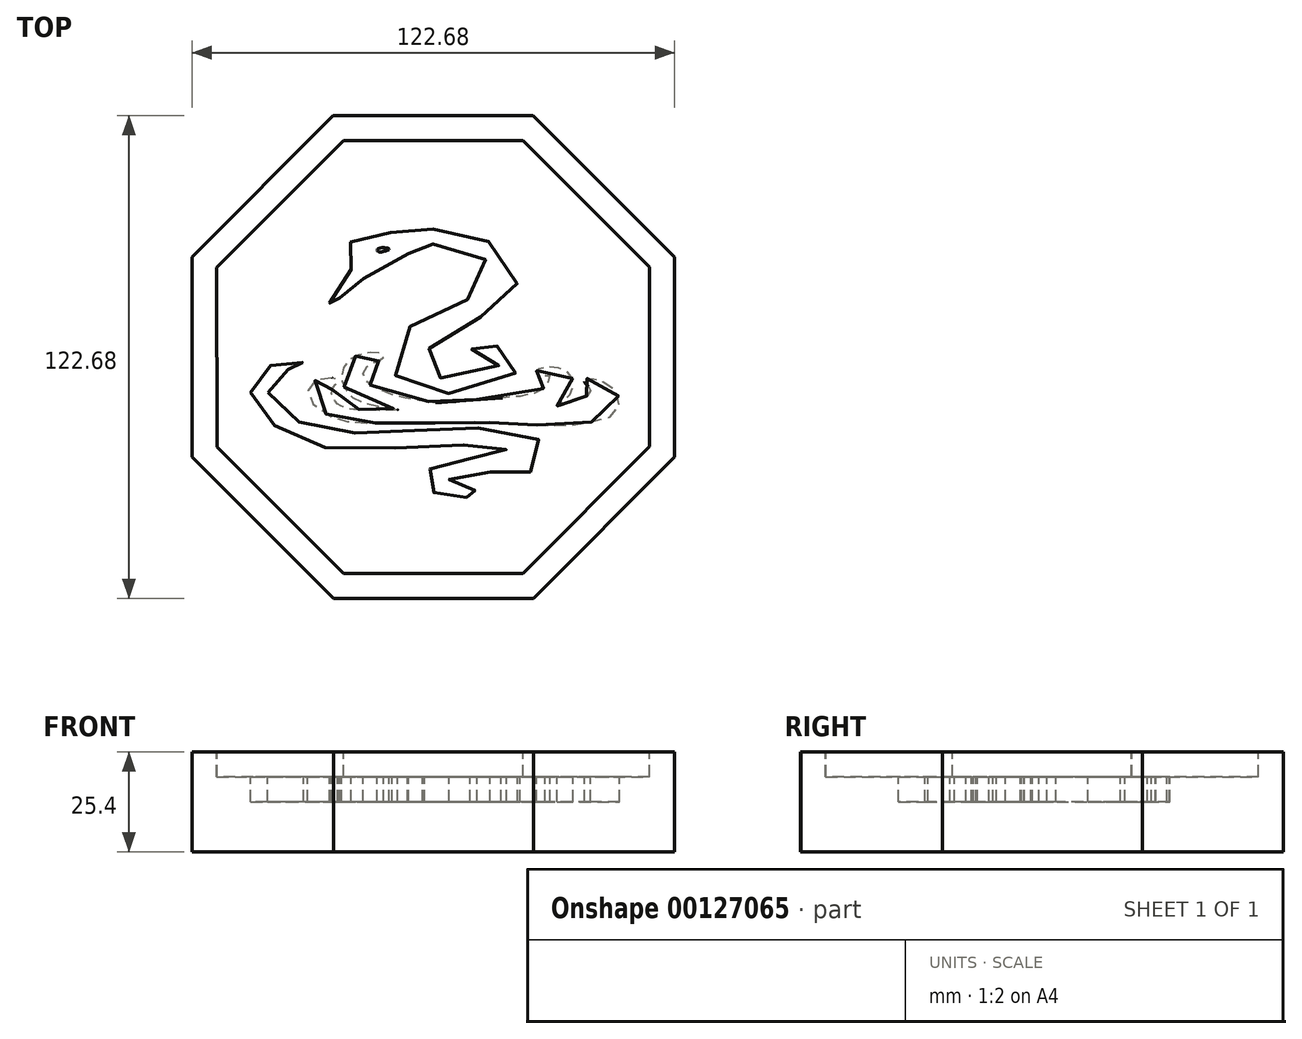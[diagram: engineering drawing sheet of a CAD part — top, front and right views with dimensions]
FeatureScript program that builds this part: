
annotation { "Feature Type Name" : "Feature", "Feature Type Description" : "" }
export const myFeature = defineFeature(function(context is Context, id is Id, definition is map)
    precondition{}
    {
        {
            var Q0;
            Q0=qCreatedBy(makeId("Top.planeOp"),FACE);
            var sketch = newSketch(context, id + "F0", { "sketchPlane" : qUnion([Q0])});
            skCircle(sketch, "E0.cCircle", {"center": v(0, 0) * mm, "radius": 61.32 * mm, "construction": true});
            skLineSegment(sketch, "E0.0", {"start": v(-61.3, -25.44) * mm, "end": v(-61.34, 25.36) * mm});
            skLineSegment(sketch, "E0.1", {"start": v(-61.34, 25.36) * mm, "end": v(-25.44, 61.3) * mm});
            skLineSegment(sketch, "E0.2", {"start": v(-25.44, 61.3) * mm, "end": v(25.36, 61.34) * mm});
            skLineSegment(sketch, "E0.3", {"start": v(25.36, 61.34) * mm, "end": v(61.3, 25.44) * mm});
            skLineSegment(sketch, "E0.4", {"start": v(61.3, 25.44) * mm, "end": v(61.34, -25.36) * mm});
            skLineSegment(sketch, "E0.5", {"start": v(61.34, -25.36) * mm, "end": v(25.44, -61.3) * mm});
            skLineSegment(sketch, "E0.6", {"start": v(25.44, -61.3) * mm, "end": v(-25.36, -61.34) * mm});
            skLineSegment(sketch, "E0.7", {"start": v(-25.36, -61.34) * mm, "end": v(-61.3, -25.44) * mm});
            skPoint(sketch, "E0.0.midPoint", {"position": v(-61.32, -0.04) * mm});
            skSolve(sketch);
        }
        {
            var Q0;
            Q0=qSketchRegion(id+"F0",true);
            extrude(context, id + "F1", {"entities" : qUnion([Q0]), "depth" : 25.4 * mm});
        }
        {
            var Q0;
            Q0=makeQuery(id+"F1.opExtrude","CAP_FACE",FACE,{"disambiguationData":[OSD([sQuery(id+"F0.wireOp",EDGE,"E0.0"),sQuery(id+"F0.wireOp",EDGE,"E0.1"),sQuery(id+"F0.wireOp",EDGE,"E0.2"),sQuery(id+"F0.wireOp",EDGE,"E0.3"),sQuery(id+"F0.wireOp",EDGE,"E0.4"),sQuery(id+"F0.wireOp",EDGE,"E0.5"),sQuery(id+"F0.wireOp",EDGE,"E0.6"),sQuery(id+"F0.wireOp",EDGE,"E0.7")])],"isStart":false});
            var sketch = newSketch(context, id + "F2", { "sketchPlane" : qUnion([Q0])});
            skLineSegment(sketch, "E1.0", {"start": v(-54.96, -22.8) * mm, "end": v(-54.99, 22.73) * mm});
            skLineSegment(sketch, "E1.1", {"start": v(-22.73, -54.99) * mm, "end": v(-54.96, -22.8) * mm});
            skLineSegment(sketch, "E1.2", {"start": v(-54.99, 22.73) * mm, "end": v(-22.8, 54.96) * mm});
            skLineSegment(sketch, "E1.3", {"start": v(22.8, -54.96) * mm, "end": v(-22.73, -54.99) * mm});
            skLineSegment(sketch, "E1.4", {"start": v(-22.8, 54.96) * mm, "end": v(22.73, 54.99) * mm});
            skLineSegment(sketch, "E1.5", {"start": v(22.73, 54.99) * mm, "end": v(54.96, 22.8) * mm});
            skLineSegment(sketch, "E1.6", {"start": v(54.96, 22.8) * mm, "end": v(54.99, -22.73) * mm});
            skLineSegment(sketch, "E1.7", {"start": v(54.99, -22.73) * mm, "end": v(22.8, -54.96) * mm});
            skSolve(sketch);
        }
        {
            var Q0;
            Q0=qSketchRegion(id+"F2",true);
            extrude(context, id + "F3", {"entities" : qUnion([Q0]), "operationType" : NewBodyOperationType.REMOVE, "oppositeDirection" : true, "depth" : 6.35 * mm});
        }
        {
            var Q0;
            Q0=makeQuery(id+"F3.boolean.opBoolean","COPY",FACE,{"derivedFrom":makeQuery(id+"F3.opExtrude","CAP_FACE",FACE,{"disambiguationData":[OSD([sQuery(id+"F2.wireOp",EDGE,"E1.0"),sQuery(id+"F2.wireOp",EDGE,"E1.1"),sQuery(id+"F2.wireOp",EDGE,"E1.2"),sQuery(id+"F2.wireOp",EDGE,"E1.3"),sQuery(id+"F2.wireOp",EDGE,"E1.4"),sQuery(id+"F2.wireOp",EDGE,"E1.5"),sQuery(id+"F2.wireOp",EDGE,"E1.6"),sQuery(id+"F2.wireOp",EDGE,"E1.7")])],"isStart":false})});
            var sketch = newSketch(context, id + "F4", { "sketchPlane" : qUnion([Q0])});
            skFitSpline(sketch, "E2", {"points": [v(0, 32.5) * mm, v(-6.29, 31.91) * mm, v(-9.41, 31.8) * mm, v(-11.5, 31.68) * mm, v(-14.27, 32.38) * mm, v(-17.62, 31.22) * mm, v(-23.64, 26.82) * mm, v(-23.4, 25.44) * mm, v(-21.56, 22.9) * mm, v(-20.86, 22.08) * mm, v(-22.71, 20.8) * mm, v(-25.72, 15.37) * mm, v(-26.3, 13.4) * mm, v(-25.72, 12.71) * mm, v(-24.91, 11.67) * mm, v(-23.99, 11.79) * mm, v(-23.99, 13.75) * mm, v(-21.21, 19.88) * mm, v(-19.01, 21.04) * mm, v(-18.2, 20.35) * mm, v(-17.05, 19.88) * mm, v(-8.65, 23.8) * mm, v(-6.28, 26.48) * mm, v(-6.49, 28.44) * mm, v(-4.53, 28.75) * mm, v(-1.44, 28.85) * mm, v(6.19, 27.72) * mm, v(12.37, 25.76) * mm, v(14.43, 20.7) * mm, v(12.48, 16.69) * mm, v(2.68, 12.26) * mm, v(-4.84, 8.44) * mm, v(-9.27, 4.22) * mm, v(-10.2, -3.2) * mm, v(-6.49, -7.74) * mm, v(2.07, -9.28) * mm, v(14.54, -7.33) * mm, v(21.75, -2.9) * mm, v(21.44, 0.92) * mm, v(18.76, 2.47) * mm, v(11.96, 3.19) * mm, v(10.41, 3.5) * mm, v(9.49, 3.19) * mm, v(9.38, 2.26) * mm, v(12.06, 1.54) * mm, v(16.9, 0) * mm, v(17.11, -1.45) * mm, v(14.23, -3.82) * mm, v(3.71, -5.47) * mm, v(-1.54, -3.92) * mm, v(-2.68, -1.14) * mm, v(-0.92, 2.26) * mm, v(5.98, 7) * mm, v(13.4, 10.92) * mm, v(19.07, 14.42) * mm, v(21.34, 18.75) * mm, v(20, 24.42) * mm, v(14.33, 29.26) * mm, v(5.45, 31.84) * mm, v(0, 32.5) * mm]});
            skFitSpline(sketch, "E3", {"points": [v(-1.17, -11.34) * mm, v(-8.33, -10.15) * mm, v(-17.05, -6.2) * mm, v(-17.7, -3.63) * mm, v(-15.5, -1.6) * mm, v(-13.84, -0.97) * mm, v(-12.64, 0) * mm, v(-13.01, 0.87) * mm, v(-17.7, 0.87) * mm, v(-22.29, -1.7) * mm, v(-23.3, -4.82) * mm, v(-23.11, -6.3) * mm, v(-20.82, -10.06) * mm, v(-13.2, -12.63) * mm, v(-9.06, -13.36) * mm, v(-13.2, -13.55) * mm, v(-19.35, -13.36) * mm, v(-23.11, -12.63) * mm, v(-25.6, -10.24) * mm, v(-25.4, -7.67) * mm, v(-24.3, -6.3) * mm, v(-25.13, -5.47) * mm, v(-29.54, -5.74) * mm, v(-31.56, -7.85) * mm, v(-31.65, -10.33) * mm, v(-26.33, -15.02) * mm, v(-21.64, -16.4) * mm, v(-14.57, -16.76) * mm, v(-4.93, -16.76) * mm, v(1.68, -16.67) * mm, v(8.38, -16.4) * mm, v(15.54, -16.76) * mm, v(20.32, -17.04) * mm, v(25.92, -17.22) * mm, v(33.08, -17.4) * mm, v(39.88, -16.58) * mm, v(45.75, -14.74) * mm, v(47.31, -11.9) * mm, v(46.12, -8.31) * mm, v(42.45, -6.02) * mm, v(40.43, -5.56) * mm, v(38.5, -5.56) * mm, v(38.5, -6.48) * mm, v(39.33, -7.4) * mm, v(39.88, -8.04) * mm, v(39.42, -9.5) * mm, v(37.77, -10.6) * mm, v(34.92, -11.53) * mm, v(33, -12.35) * mm, v(31.43, -12.35) * mm, v(33.36, -10.88) * mm, v(35.1, -8.96) * mm, v(35.38, -5.65) * mm, v(33.17, -3.26) * mm, v(28.03, -2.62) * mm, v(26.2, -3.63) * mm, v(27.2, -4.64) * mm, v(29.5, -4.64) * mm, v(29.04, -6.57) * mm, v(26.2, -9.05) * mm, v(13.98, -10.6) * mm, v(1.96, -11.53) * mm, v(0, -11.53) * mm, v(-1.17, -11.34) * mm]});
            skFitSpline(sketch, "E4", {"points": [v(-41.97, -9.01) * mm, v(-41.97, -7.37) * mm, v(-38.42, -3.9) * mm, v(-34.6, -2.77) * mm, v(-33.48, -2.77) * mm, v(-32.96, -2.17) * mm, v(-33.13, -1.47) * mm, v(-35.82, -0.78) * mm, v(-39.98, -1.56) * mm, v(-44.57, -4.25) * mm, v(-46.4, -7.89) * mm, v(-45, -13.09) * mm, v(-39.6, -17.94) * mm, v(-29.87, -22.5) * mm, v(-12.88, -23.2) * mm, v(4.8, -22.42) * mm, v(16.54, -22.57) * mm, v(18.54, -23.5) * mm, v(15.69, -25.05) * mm, v(9.2, -25.82) * mm, v(1.4, -27.28) * mm, v(-1.53, -29.21) * mm, v(-2.07, -32.46) * mm, v(0, -34.39) * mm, v(1.56, -34.85) * mm, v(6.73, -35.31) * mm, v(10.13, -36.24) * mm, v(10.9, -36.47) * mm, v(11.13, -35.4) * mm, v(10.36, -33.7) * mm, v(6.04, -31.92) * mm, v(4.1, -31.6) * mm, v(4.8, -30.14) * mm, v(12.98, -29.06) * mm, v(19.86, -29.68) * mm, v(24.95, -29.06) * mm, v(28.35, -24.5) * mm, v(25.1, -19.87) * mm, v(9.51, -18.02) * mm, v(-4.85, -18.64) * mm, v(-17.67, -19.4) * mm, v(-29.64, -17.79) * mm, v(-38.9, -13.85) * mm, v(-41.97, -9.01) * mm]});
            skFitSpline(sketch, "E5", {"points": [v(-11.19, 27.42) * mm, v(-13.77, 27.64) * mm, v(-14.17, 26.9) * mm, v(-13.26, 26.7) * mm, v(-12.46, 26.87) * mm, v(-11.19, 27.42) * mm]});
            skSolve(sketch);
        }
        {
            var Q0;
            Q0 = qSketchRegion(id + "F4", true);
            extrude(context, id + "F5", {"entities" : qUnion([Q0]), "operationType" : NewBodyOperationType.REMOVE, "oppositeDirection" : true, "depth" : 6.35 * mm});
        }
    });
